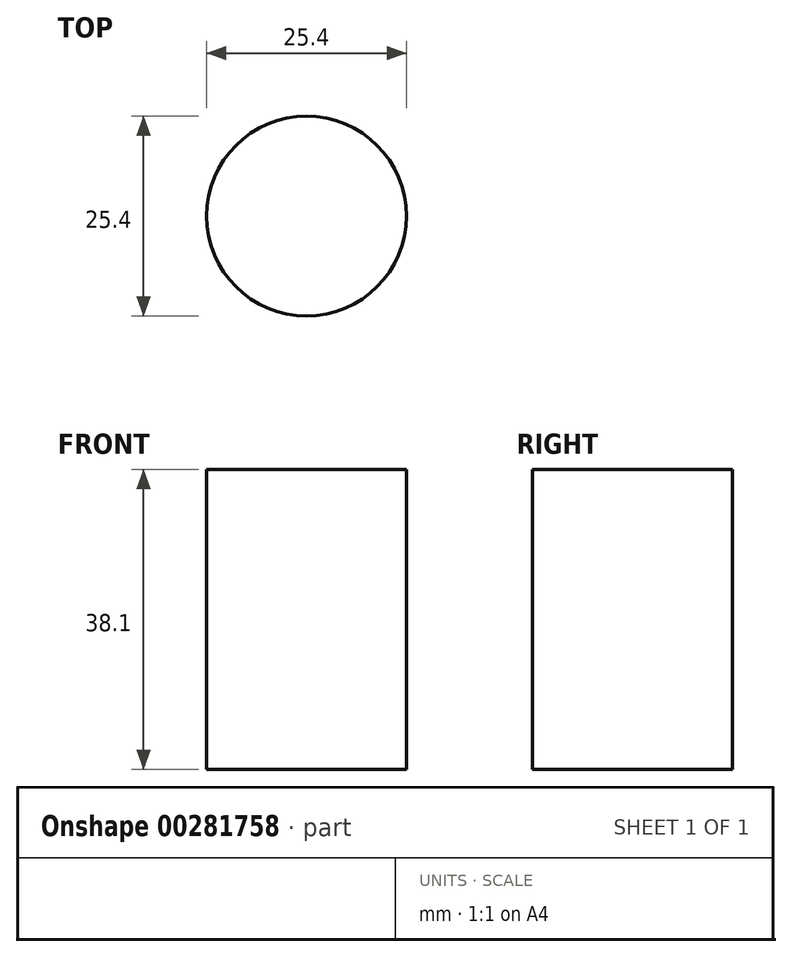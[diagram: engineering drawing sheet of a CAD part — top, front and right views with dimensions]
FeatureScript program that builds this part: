
annotation { "Feature Type Name" : "Feature", "Feature Type Description" : "" }
export const myFeature = defineFeature(function(context is Context, id is Id, definition is map)
    precondition{}
    {
        {
            var Q0;
            Q0=qCreatedBy(makeId("Top.planeOp"),FACE);
            var sketch = newSketch(context, id + "F0", { "sketchPlane" : qUnion([Q0])});
            skCircle(sketch, "E0", {"center": v(-30.38, 22.26) * mm, "radius": 12.7 * mm});
            skSolve(sketch);
        }
        {
            var Q0;
            Q0=makeQuery(id+"F0.imprint","IMPRINT",FACE,{"disambiguationData":[TD([[makeQuery(id+"F0.imprint","IMPRINT",EDGE,{"derivedFrom":sQuery(id+"F0.wireOp",EDGE,"E0")}),1.0]])]});
            extrude(context, id + "F1", {"entities" : qUnion([Q0]), "depth" : 38.1 * mm});
        }
    });
